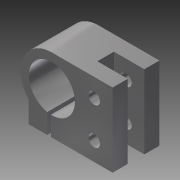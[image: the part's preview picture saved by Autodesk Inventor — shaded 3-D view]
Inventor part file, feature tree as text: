
AUTODESK INVENTOR PART (.ipt)
format: ipt  version: 2015 (Build 190159000, 159)  size: 145,920 bytes
history: native  units: mm
features: extrude x2, sketch x2
ambient origin geometry x8: Origin, YZ Plane, XZ Plane, XY Plane, X Axis, Y Axis, Z Axis, Center Point
bodies: Solid1 (feature_tree)
feature tree (4):
  extrude  "Extrusion1"  Depth=25.4mm TaperAngle=0.0deg
  extrude  "Extrusion2"  [1 undecoded]
  sketch  "Sketch1"  dims[d0=50.0mm d1=40.0mm d2=10.0mm d3=10.0mm d4=20.0mm d5=6.2mm d6=6.2mm d7=45.5mm d8=35.5mm d9=4.5mm d10=4.5mm d11=12.5mm d12=12.5mm d13=2.0mm d14=25.4mm d15=0.0mm]
  sketch  "Sketch2"  dims[d16=8.2mm d17=16.5mm d18=9.0mm d19=25.4mm d20=0.0mm]
note: 1 required parameter value undecoded (feature->parameter linkage not recoverable at this tier; creation-order binding heuristic only, values carry confidence <= 0.55)
